# Revit family: REVIT-CONQ OUTDOOR 40-80-130
name_source: partatom
category: Mechanical Equipment
revit_build: Autodesk Revit 2017 (Build: 20190507_1515(x64)
units: mm (PartAtom-declared; Revit-internal decimal feet)

## family parameters
Always vertical = No
Cut with Voids When Loaded = No
OmniClass Number = 23.75.00.00
OmniClass Title = Climate Control (HVAC)
Part Type = Normal
Room Calculation Point = No
Round Connector Dimension = Use Radius
Shared = No
Work Plane-Based = No

## types (5) — shared parameters
Assembly Code = D3020100
BuildingReturn = 1"
BuildingReturnHeight = 46 1/2"
BuildingReturnLength = 17 7/8"
BuildingReturnRadius = 1/2"
ColdInlet = 2"
ColdInletHeight = 12"
ColdWaterInletExtension = 17 7/8"
ColdWaterInletRadius = 1"
ColdWaterReturnHeight = 46 1/2"
CondensateDrain = 1/2"
CondensateDrainCenterOffset = 6 1/8"
CondensateDrainConnectionRadius = 1/4"
CondensateDrainHeight = 1 1/2"
CondensateDrainLengthOffset = 32"
ControlEnclosureExtension = 20 1/8"
ControlPanelHeight = 49"
ControlPanelLength = 8"
ControlPanelWidth = 14"
Current = 11.0 A
Description = Conquest® Semi-Instantaneous Outdoor Condensing Water Heater
DrainHeight = 12"
DrainPipeRadius = 1/2"
DrainValve = 1"
ElectricalServiceConnectionRadius = 1/2"
EnclosureCoverExtension = 25 1/4"
FlueBoxConnectCenter = 21 1/2"
FlueBoxWidth = 9 1/2"
FlueConnection = 6 5/8"
FlueConnectionRadius = 3 3/8"
FlueConnectionWallRadius = 3 1/8"
Frequency = 60.00 Hz
GasConnectionExtension = 18 3/8"
GasConnectionHeight = 74 3/8"
GasConnectionToFront = 9 1/4"
HotOutletHeight = 76 3/8"
HotOutletToRear = 0"
HotWaterCenterOffset = 10 1/4"
HotWaterOutlet = 2"
HotWaterOutletLength = 82"
HotWaterOutletRadius = 1"
Manufacturer = PVI Industries, LLC
Maximum Static Pressure = 14.0" W.C.
Modeling Code = ABO090507TAS1507ABC0905
Normal = 90.00°
Number of Poles = 1
OmniClass Code = 23.65.35.11.11
OmniClass Title = Storage Water Heater
OperatingWeight = 1800
Piping Material = Copper Pipe
ReliefValve = 1"
ReliefValveHeight = 61 3/4"
ReliefValveRadius = 1/2"
Storage Capacity = 130 CF
Tank Casing = <By Category>
TankDiameter = 33 5/8"
TankHeight = 81"
TankRadius = 16 7/8"
URL = www.pvi.com
Version = 1.0
Voltage = 120 V
Weight Units = lbs.

## per-type parameters (varying)
| type | GPH Recovery Rate at 40F to 140F | GPH Recovery Rate at 70F to 140F | GasConnection | GasConnectionRadius | Input Btu/h | Model |
| Conquest Condensing 40 L 130A-GCLMW | 471 | 657 | 3/4" | 3/8" | 399000 Btu/h | 40 L 130A-GCLMW |
| Conquest Condensing 50 L 130A-GCLMW | 588 | 823 | 1" | 1/2" | 500000 Btu/h | 50 L 130A-GCLMW |
| Conquest Condensing 60 L 130A-GCLMW | 699 | 988 | 1" | 1/2" | 600000 Btu/h | 60 L 130A-GCLMW |
| Conquest Condensing 70 L 130A-GCLMW | 815 | 1152 | 1" | 1/2" | 700000 Btu/h | 70 L 130A-GCLMW |
| Conquest Condensing 80 L 130A-GCLMW | 932 | 1317 | 1" | 1/2" | 800000 Btu/h | 80 L 130A-GCLMW |

## geometry (parser evidence)
native form markers: Blend x10, Sweep x2
no freeform markers — native parametric forms only
